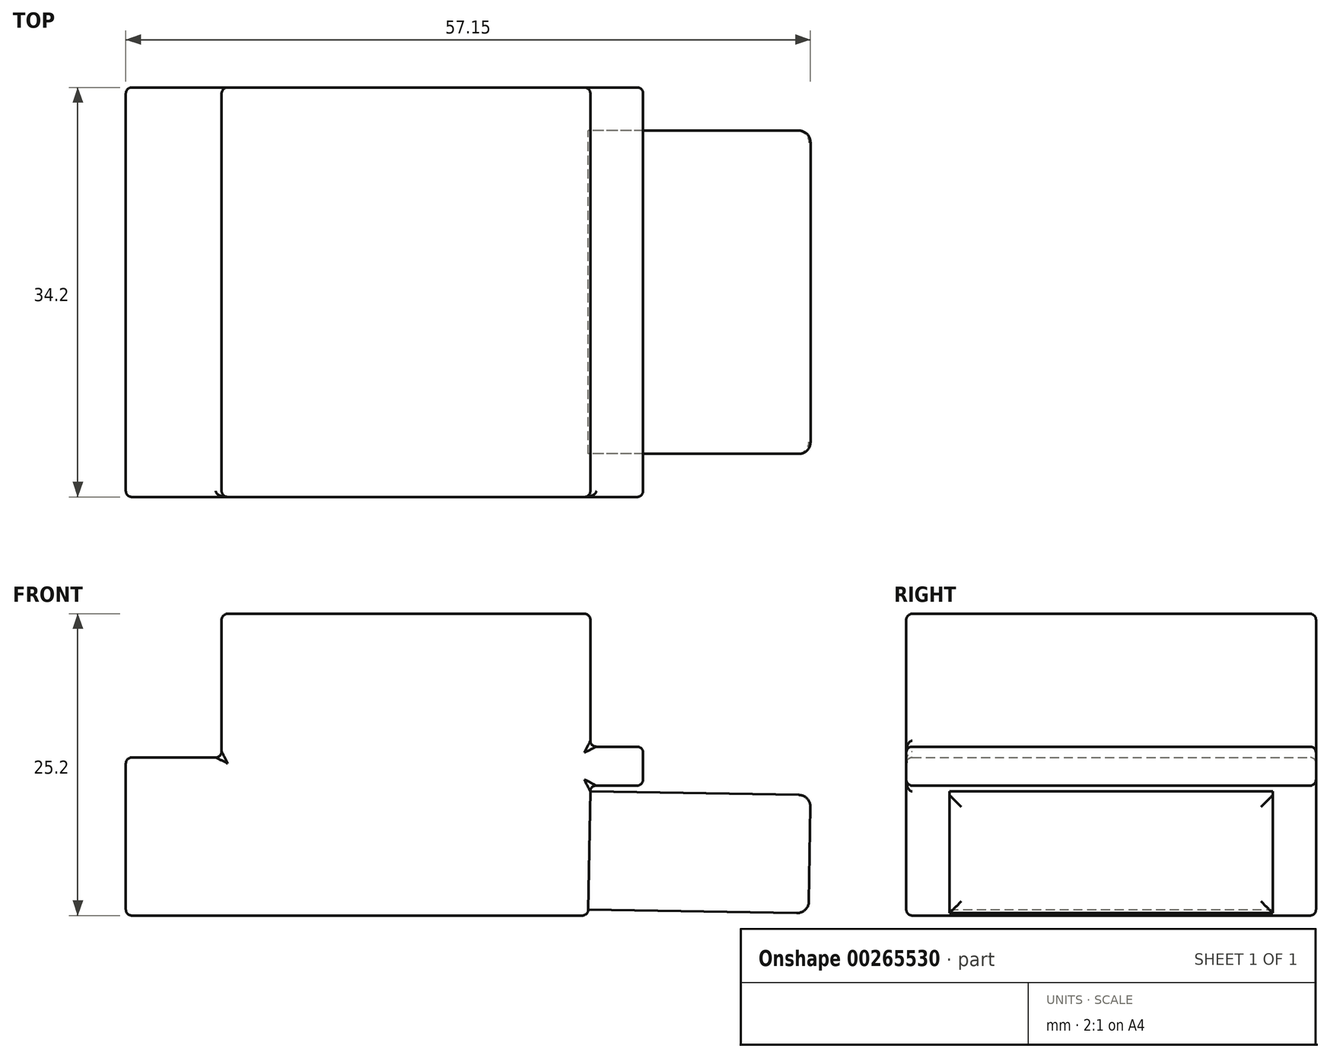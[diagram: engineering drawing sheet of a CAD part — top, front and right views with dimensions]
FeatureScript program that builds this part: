
annotation { "Feature Type Name" : "Feature", "Feature Type Description" : "" }
export const myFeature = defineFeature(function(context is Context, id is Id, definition is map)
    precondition{}
    {
        {
            var Q0;
            Q0=qCreatedBy(makeId("Front.planeOp"),FACE);
            var sketch = newSketch(context, id + "F0", { "sketchPlane" : qUnion([Q0])});
            skLineSegment(sketch, "E0", {"start": v(0, 0) * mm, "end": v(38.6, 0) * mm});
            skLineSegment(sketch, "E1", {"start": v(0, 0) * mm, "end": v(0, 13.2) * mm});
            skLineSegment(sketch, "E2", {"start": v(0, 13.2) * mm, "end": v(8, 13.2) * mm});
            skLineSegment(sketch, "E3", {"start": v(8, 13.2) * mm, "end": v(8, 25.2) * mm});
            skLineSegment(sketch, "E4", {"start": v(8, 25.2) * mm, "end": v(38.78, 25.2) * mm});
            skLineSegment(sketch, "E5", {"start": v(38.78, 25.2) * mm, "end": v(38.78, 14.1) * mm});
            skLineSegment(sketch, "E6", {"start": v(38.78, 14.1) * mm, "end": v(43.18, 14.1) * mm});
            skLineSegment(sketch, "E7", {"start": v(43.18, 14.1) * mm, "end": v(43.18, 10.85) * mm});
            skLineSegment(sketch, "E8", {"start": v(43.18, 10.85) * mm, "end": v(38.78, 10.85) * mm});
            skLineSegment(sketch, "E9", {"start": v(38.78, 10.85) * mm, "end": v(38.6, 0) * mm});
            skSolve(sketch);
        }
        {
            var Q0;
            Q0=makeQuery(id+"F0.imprint","IMPRINT",FACE,{"disambiguationData":[TD([[makeQuery(id+"F0.imprint","IMPRINT",EDGE,{"derivedFrom":sQuery(id+"F0.wireOp",EDGE,"E0")}),1.0]])]});
            extrude(context, id + "F1", {"entities" : qUnion([Q0]), "depth" : 34.2 * mm});
        }
        {
            var Q0;
            Q0=makeQuery(id+"F1.opExtrude","CAP_FACE",FACE,{"disambiguationData":[OSD([sQuery(id+"F0.wireOp",EDGE,"E0"),sQuery(id+"F0.wireOp",EDGE,"E1"),sQuery(id+"F0.wireOp",EDGE,"E2"),sQuery(id+"F0.wireOp",EDGE,"E3"),sQuery(id+"F0.wireOp",EDGE,"E4"),sQuery(id+"F0.wireOp",EDGE,"E5"),sQuery(id+"F0.wireOp",EDGE,"E6"),sQuery(id+"F0.wireOp",EDGE,"E7"),sQuery(id+"F0.wireOp",EDGE,"E8"),sQuery(id+"F0.wireOp",EDGE,"E9")])],"isStart":false});
            fillet(context, id + "F2", {"entities" : qUnion([Q0]), "radius" : 0.5 * mm, "tangentPropagation" : true, "allowEdgeOverflow" : false});
        }
        {
            var Q0;
            Q0=makeQuery(id+"F1.opExtrude","SWEPT_FACE",FACE,{"disambiguationData":[OSD([sQuery(id+"F0.wireOp",EDGE,"E4")])]});
            var Q1;
            Q1=makeQuery(id+"F1.opExtrude","SWEPT_FACE",FACE,{"disambiguationData":[OSD([sQuery(id+"F0.wireOp",EDGE,"E5")])]});
            var Q2;
            Q2=makeQuery(id+"F1.opExtrude","SWEPT_FACE",FACE,{"disambiguationData":[OSD([sQuery(id+"F0.wireOp",EDGE,"E7")])]});
            var Q3;
            Q3=makeQuery(id+"F1.opExtrude","SWEPT_FACE",FACE,{"disambiguationData":[OSD([sQuery(id+"F0.wireOp",EDGE,"E9")])]});
            var Q4;
            Q4=makeQuery(id+"F1.opExtrude","SWEPT_FACE",FACE,{"disambiguationData":[OSD([sQuery(id+"F0.wireOp",EDGE,"E6")])]});
            var Q5;
            Q5=makeQuery(id+"F1.opExtrude","SWEPT_FACE",FACE,{"disambiguationData":[OSD([sQuery(id+"F0.wireOp",EDGE,"E0")])]});
            var Q6;
            Q6=makeQuery(id+"F1.opExtrude","CAP_FACE",FACE,{"disambiguationData":[OSD([sQuery(id+"F0.wireOp",EDGE,"E0"),sQuery(id+"F0.wireOp",EDGE,"E1"),sQuery(id+"F0.wireOp",EDGE,"E2"),sQuery(id+"F0.wireOp",EDGE,"E3"),sQuery(id+"F0.wireOp",EDGE,"E4"),sQuery(id+"F0.wireOp",EDGE,"E5"),sQuery(id+"F0.wireOp",EDGE,"E6"),sQuery(id+"F0.wireOp",EDGE,"E7"),sQuery(id+"F0.wireOp",EDGE,"E8"),sQuery(id+"F0.wireOp",EDGE,"E9")])],"isStart":true});
            var Q7;
            Q7=makeQuery(id+"F1.opExtrude","SWEPT_FACE",FACE,{"disambiguationData":[OSD([sQuery(id+"F0.wireOp",EDGE,"E8")])]});
            var Q8;
            Q8=makeQuery(id+"F1.opExtrude","SWEPT_FACE",FACE,{"disambiguationData":[OSD([sQuery(id+"F0.wireOp",EDGE,"E3")])]});
            var Q9;
            Q9=makeQuery(id+"F1.opExtrude","SWEPT_FACE",FACE,{"disambiguationData":[OSD([sQuery(id+"F0.wireOp",EDGE,"E1")])]});
            var Q10;
            Q10=makeQuery(id+"F1.opExtrude","SWEPT_FACE",FACE,{"disambiguationData":[OSD([sQuery(id+"F0.wireOp",EDGE,"E2")])]});
            var Q11;
            Q11=makeQuery(id+"F1.opExtrude","CAP_FACE",FACE,{"disambiguationData":[OSD([sQuery(id+"F0.wireOp",EDGE,"E0"),sQuery(id+"F0.wireOp",EDGE,"E1"),sQuery(id+"F0.wireOp",EDGE,"E2"),sQuery(id+"F0.wireOp",EDGE,"E3"),sQuery(id+"F0.wireOp",EDGE,"E4"),sQuery(id+"F0.wireOp",EDGE,"E5"),sQuery(id+"F0.wireOp",EDGE,"E6"),sQuery(id+"F0.wireOp",EDGE,"E7"),sQuery(id+"F0.wireOp",EDGE,"E8"),sQuery(id+"F0.wireOp",EDGE,"E9")])],"isStart":false});
            fillet(context, id + "F3", {"entities" : qUnion([Q0, Q1, Q2, Q3, Q4, Q5, Q6, Q7, Q8, Q9, Q10, Q11]), "radius" : 0.5 * mm, "tangentPropagation" : true, "allowEdgeOverflow" : false});
        }
        {
            var Q0;
            Q0=makeQuery(id+"F1.opExtrude","SWEPT_FACE",FACE,{"disambiguationData":[OSD([sQuery(id+"F0.wireOp",EDGE,"E9")])]});
            var sketch = newSketch(context, id + "F4", { "sketchPlane" : qUnion([Q0])});
            skLineSegment(sketch, "E10", {"start": v(-17.1, 11) * mm, "end": v(-3.6, 11) * mm, "construction": true});
            skLineSegment(sketch, "E11.bottom", {"start": v(-3.6, 11) * mm, "end": v(-30.6, 11) * mm});
            skLineSegment(sketch, "E11.top", {"start": v(-3.6, 1.13) * mm, "end": v(-30.6, 1.13) * mm});
            skLineSegment(sketch, "E11.left", {"start": v(-3.6, 11) * mm, "end": v(-3.6, 1.13) * mm});
            skLineSegment(sketch, "E11.right", {"start": v(-30.6, 11) * mm, "end": v(-30.6, 1.13) * mm});
            skSolve(sketch);
        }
        {
            var Q0;
            Q0=makeQuery(id+"F4.imprint","IMPRINT",FACE,{"disambiguationData":[TD([[makeQuery(id+"F4.imprint","IMPRINT",EDGE,{"derivedFrom":sQuery(id+"F4.wireOp",EDGE,"E11.bottom")}),1.0]])]});
            extrude(context, id + "F5", {"entities" : qUnion([Q0]), "operationType" : NewBodyOperationType.ADD, "depth" : 18.4 * mm});
        }
        {
            var Q0;
            Q0=makeQuery(id+"F5.opExtrude","CAP_FACE",FACE,{"disambiguationData":[OSD([sQuery(id+"F4.wireOp",EDGE,"E11.bottom"),sQuery(id+"F4.wireOp",EDGE,"E11.top"),sQuery(id+"F4.wireOp",EDGE,"E11.left"),sQuery(id+"F4.wireOp",EDGE,"E11.right")])],"isStart":false});
            fillet(context, id + "F6", {"entities" : qUnion([Q0]), "radius" : 1 * mm, "tangentPropagation" : true, "allowEdgeOverflow" : false});
        }
    });
